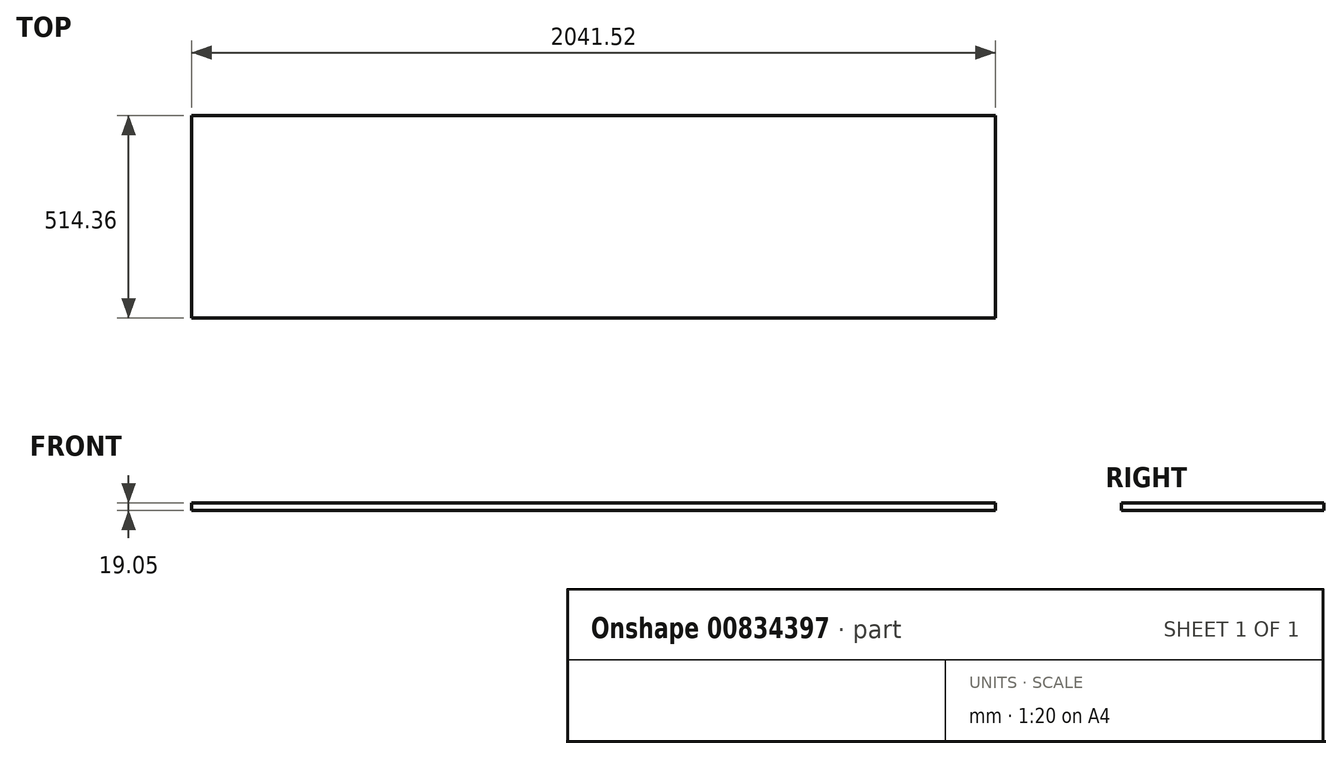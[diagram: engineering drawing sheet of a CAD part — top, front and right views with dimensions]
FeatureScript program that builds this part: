
annotation { "Feature Type Name" : "Feature", "Feature Type Description" : "" }
export const myFeature = defineFeature(function(context is Context, id is Id, definition is map)
    precondition{}
    {
        {
            var Q0;
            Q0=qCreatedBy(makeId("Top.planeOp"),FACE);
            var sketch = newSketch(context, id + "F0", { "sketchPlane" : qUnion([Q0])});
            skLineSegment(sketch, "E0.0", {"start": v(1020.76, 257.18) * mm, "end": v(1020.76, -257.18) * mm});
            skLineSegment(sketch, "E1.0", {"start": v(-1020.76, 257.17) * mm, "end": v(-1020.76, -257.18) * mm});
            skLineSegment(sketch, "E2", {"start": v(-1020.76, -257.18) * mm, "end": v(1020.76, -257.18) * mm});
            skLineSegment(sketch, "E3", {"start": v(-1020.76, 257.18) * mm, "end": v(1020.76, 257.18) * mm});
            skSolve(sketch);
        }
        {
            var Q0;
            Q0=makeQuery(id+"F0.imprint","IMPRINT",FACE,{"disambiguationData":[TD([[makeQuery(id+"F0.imprint","IMPRINT",EDGE,{"derivedFrom":sQuery(id+"F0.wireOp",EDGE,"E0.0")}),-1.0]])]});
            extrude(context, id + "F1", {"entities" : qUnion([Q0]), "oppositeDirection" : true, "depth" : 19.05 * mm, "offsetDistance" : 25.4 * mm});
        }
    });
